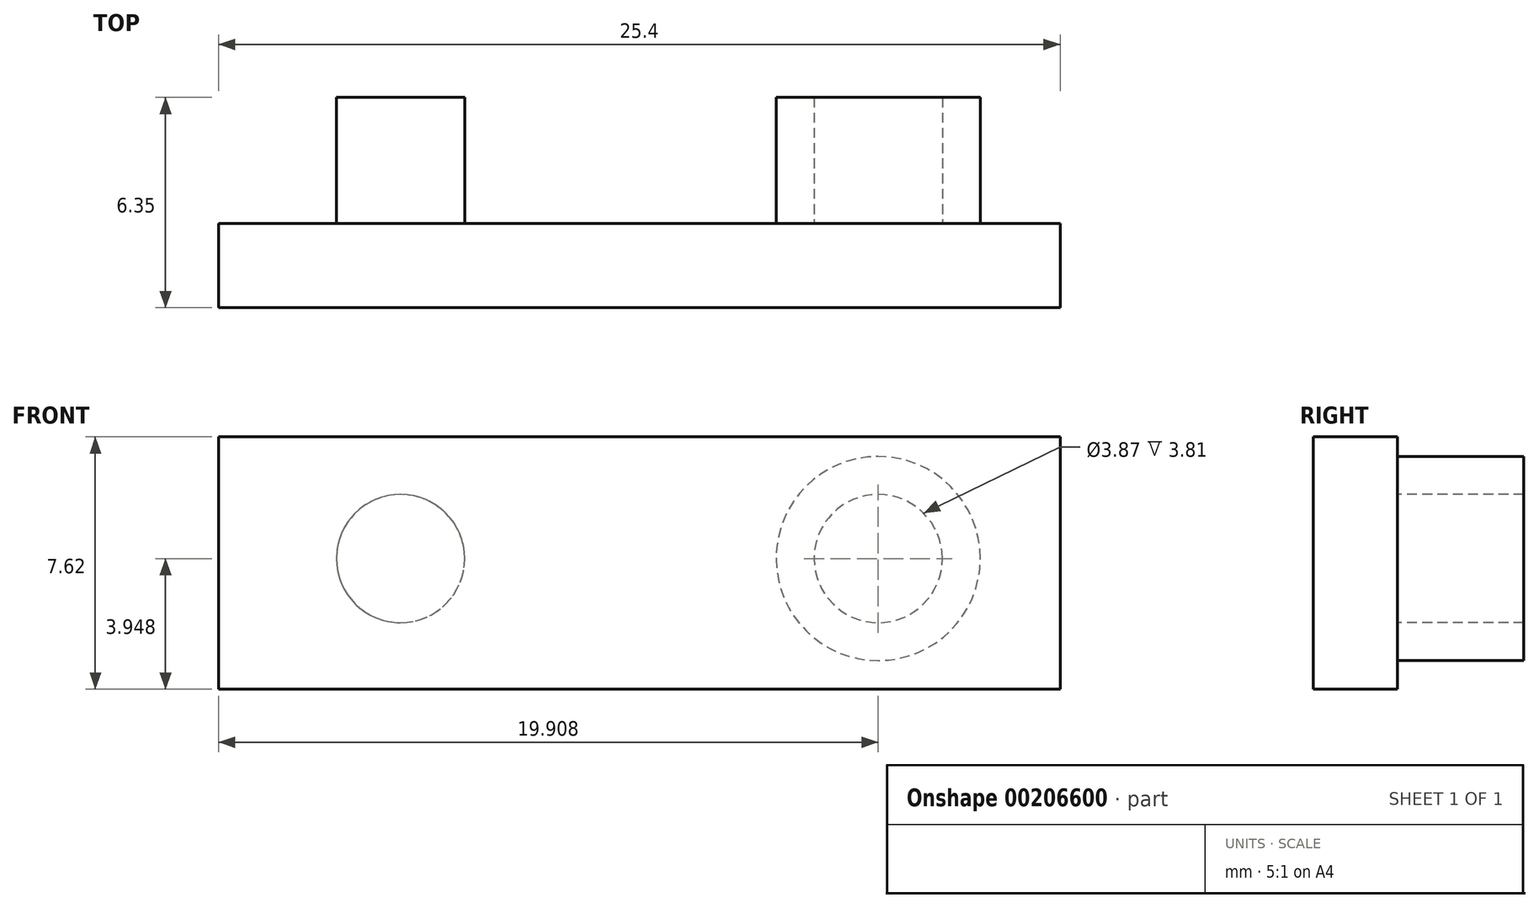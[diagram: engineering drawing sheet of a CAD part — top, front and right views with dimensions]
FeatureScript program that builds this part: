
annotation { "Feature Type Name" : "Feature", "Feature Type Description" : "" }
export const myFeature = defineFeature(function(context is Context, id is Id, definition is map)
    precondition{}
    {
        {
            var Q0;
            Q0=qCreatedBy(makeId("Front.planeOp"),FACE);
            var sketch = newSketch(context, id + "F0", { "sketchPlane" : qUnion([Q0])});
            skLineSegment(sketch, "E0.bottom", {"start": v(12.7, -2.79) * mm, "end": v(-12.7, -2.79) * mm});
            skLineSegment(sketch, "E0.top", {"start": v(12.7, -10.4) * mm, "end": v(-12.7, -10.4) * mm});
            skLineSegment(sketch, "E0.left", {"start": v(12.7, -2.79) * mm, "end": v(12.7, -10.4) * mm});
            skLineSegment(sketch, "E0.right", {"start": v(-12.7, -2.79) * mm, "end": v(-12.7, -10.4) * mm});
            skLineSegment(sketch, "E1", {"start": v(0, -10.4) * mm, "end": v(12.7, -10.4) * mm});
            skLineSegment(sketch, "E2", {"start": v(0, -10.4) * mm, "end": v(-12.7, -10.4) * mm});
            skSolve(sketch);
        }
        {
            var Q0;
            Q0=makeQuery(id+"F0.imprint","IMPRINT",FACE,{"disambiguationData":[TD([[makeQuery(id+"F0.imprint","IMPRINT",EDGE,{"derivedFrom":sQuery(id+"F0.wireOp",EDGE,"E0.bottom")}),1.0]])]});
            extrude(context, id + "F1", {"entities" : qUnion([Q0]), "depth" : 2.54 * mm});
        }
        {
            var Q0;
            Q0=makeQuery(id+"F1.opExtrude","CAP_FACE",FACE,{"disambiguationData":[OSD([sQuery(id+"F0.wireOp",EDGE,"E0.bottom"),sQuery(id+"F0.wireOp",EDGE,"E0.left"),sQuery(id+"F0.wireOp",EDGE,"E0.right"),sQuery(id+"F0.wireOp",EDGE,"E1"),sQuery(id+"F0.wireOp",EDGE,"E2")])],"isStart":true});
            var sketch = newSketch(context, id + "F2", { "sketchPlane" : qUnion([Q0])});
            skCircle(sketch, "E3", {"center": v(-7.2, -6.46) * mm, "radius": 3.08 * mm});
            skCircle(sketch, "E4", {"center": v(-7.2, -6.46) * mm, "radius": 1.94 * mm});
            skCircle(sketch, "E5.MirrorC", {"center": v(7.2, -6.46) * mm, "radius": 1.94 * mm});
            skCircle(sketch, "E6.MirrorC", {"center": v(7.2, -6.46) * mm, "radius": 3.08 * mm});
            skSolve(sketch);
        }
        {
            var Q0;
            Q0=makeQuery(id+"F2.imprint","IMPRINT",FACE,{"disambiguationData":[TD([[makeQuery(id+"F2.imprint","IMPRINT",EDGE,{"derivedFrom":sQuery(id+"F2.wireOp",EDGE,"E3")}),1.0]])]});
            var Q1;
            Q1=makeQuery(id+"F2.imprint","IMPRINT",FACE,{"disambiguationData":[TD([[makeQuery(id+"F2.imprint","IMPRINT",EDGE,{"derivedFrom":sQuery(id+"F2.wireOp",EDGE,"E5.MirrorC")}),1.0]])]});
            extrude(context, id + "F3", {"entities" : qUnion([Q0, Q1]), "operationType" : NewBodyOperationType.ADD, "depth" : 3.8 * mm});
        }
    });
